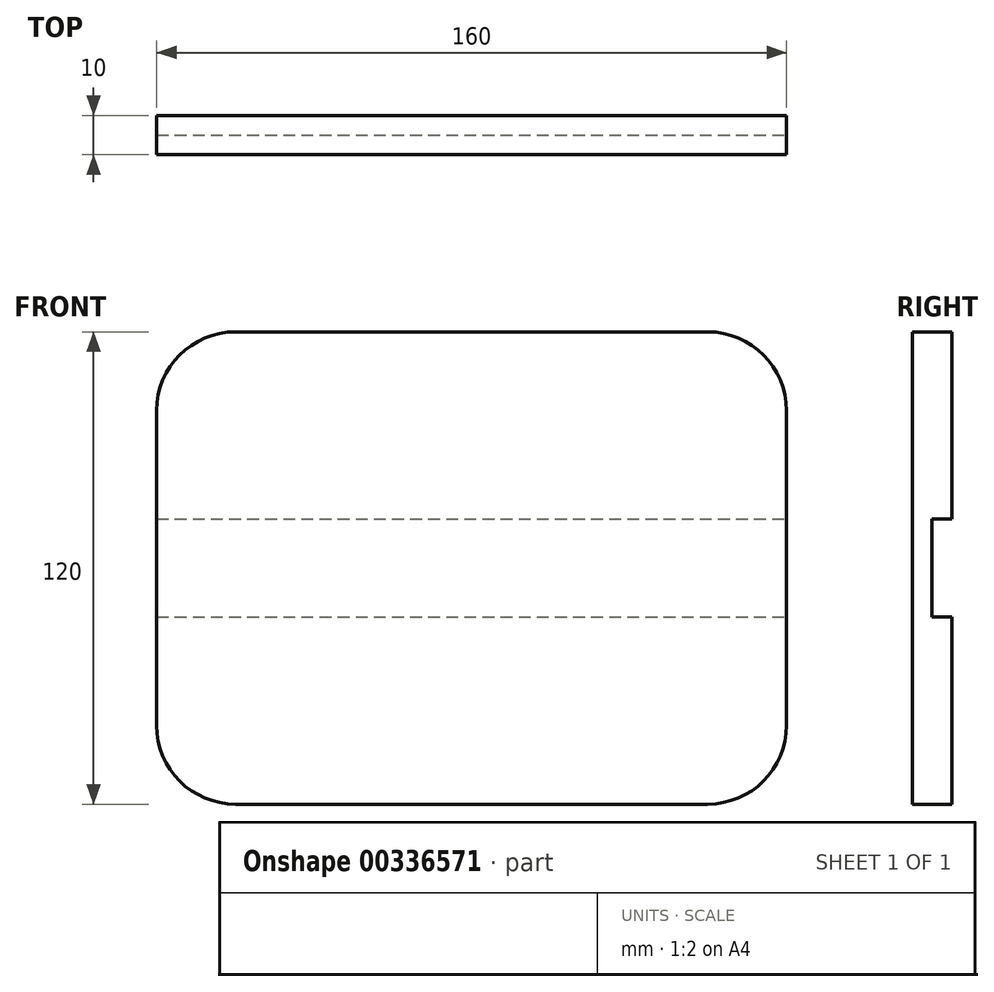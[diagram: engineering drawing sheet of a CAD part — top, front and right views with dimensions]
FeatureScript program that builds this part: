
annotation { "Feature Type Name" : "Feature", "Feature Type Description" : "" }
export const myFeature = defineFeature(function(context is Context, id is Id, definition is map)
    precondition{}
    {
        {
            var Q0;
            Q0=qCreatedBy(makeId("Front.planeOp"),FACE);
            var sketch = newSketch(context, id + "F0", { "sketchPlane" : qUnion([Q0])});
            skLineSegment(sketch, "E0.bottom", {"start": v(-80, 60) * mm, "end": v(80, 60) * mm});
            skLineSegment(sketch, "E0.top", {"start": v(-80, -60) * mm, "end": v(80, -60) * mm});
            skLineSegment(sketch, "E0.left", {"start": v(-80, 60) * mm, "end": v(-80, -60) * mm});
            skLineSegment(sketch, "E0.right", {"start": v(80, 60) * mm, "end": v(80, -60) * mm});
            skPoint(sketch, "E0.middle", {"position": v(0, 0) * mm});
            skSolve(sketch);
        }
        {
            var Q0;
            Q0=qCreatedBy(makeId("Front.planeOp"),FACE);
            var sketch = newSketch(context, id + "F1", { "sketchPlane" : qUnion([Q0])});
            skLineSegment(sketch, "E1.bottom", {"start": v(-85, 12.5) * mm, "end": v(85, 12.5) * mm});
            skLineSegment(sketch, "E1.top", {"start": v(-85, -12.5) * mm, "end": v(85, -12.5) * mm});
            skLineSegment(sketch, "E1.left", {"start": v(-85, 12.5) * mm, "end": v(-85, -12.5) * mm});
            skLineSegment(sketch, "E1.right", {"start": v(85, 12.5) * mm, "end": v(85, -12.5) * mm});
            skPoint(sketch, "E1.middle", {"position": v(0, 0) * mm});
            skSolve(sketch);
        }
        {
            var Q0;
            Q0=makeQuery(id+"F0.imprint","IMPRINT",FACE,{"disambiguationData":[TD([[makeQuery(id+"F0.imprint","IMPRINT",EDGE,{"derivedFrom":sQuery(id+"F0.wireOp",EDGE,"E0.bottom")}),-1.0]])]});
            extrude(context, id + "F2", {"entities" : qUnion([Q0]), "depth" : 10 * mm});
        }
        {
            var Q0;
            Q0 = qSketchRegion(id + "F1", true);
            extrude(context, id + "F3", {"entities" : qUnion([Q0]), "operationType" : NewBodyOperationType.REMOVE, "depth" : 5 * mm});
        }
        {
            var Q0;
            Q0=makeQuery(id+"F2.opExtrude","SWEPT_EDGE",EDGE,{"disambiguationData":[OSD([sQuery(id+"F0.wireOp",EDGE,"E0.top"),sQuery(id+"F0.wireOp",EDGE,"E0.right")])]});
            var Q1;
            Q1=makeQuery(id+"F2.opExtrude","SWEPT_EDGE",EDGE,{"disambiguationData":[OSD([sQuery(id+"F0.wireOp",EDGE,"E0.bottom"),sQuery(id+"F0.wireOp",EDGE,"E0.right")])]});
            var Q2;
            Q2=makeQuery(id+"F2.opExtrude","SWEPT_EDGE",EDGE,{"disambiguationData":[OSD([sQuery(id+"F0.wireOp",EDGE,"E0.bottom"),sQuery(id+"F0.wireOp",EDGE,"E0.left")])]});
            var Q3;
            Q3=makeQuery(id+"F2.opExtrude","SWEPT_EDGE",EDGE,{"disambiguationData":[OSD([sQuery(id+"F0.wireOp",EDGE,"E0.top"),sQuery(id+"F0.wireOp",EDGE,"E0.left")])]});
            fillet(context, id + "F4", {"entities" : qUnion([Q0, Q1, Q2, Q3]), "radius" : 20 * mm, "tangentPropagation" : true, "allowEdgeOverflow" : false});
        }
    });
